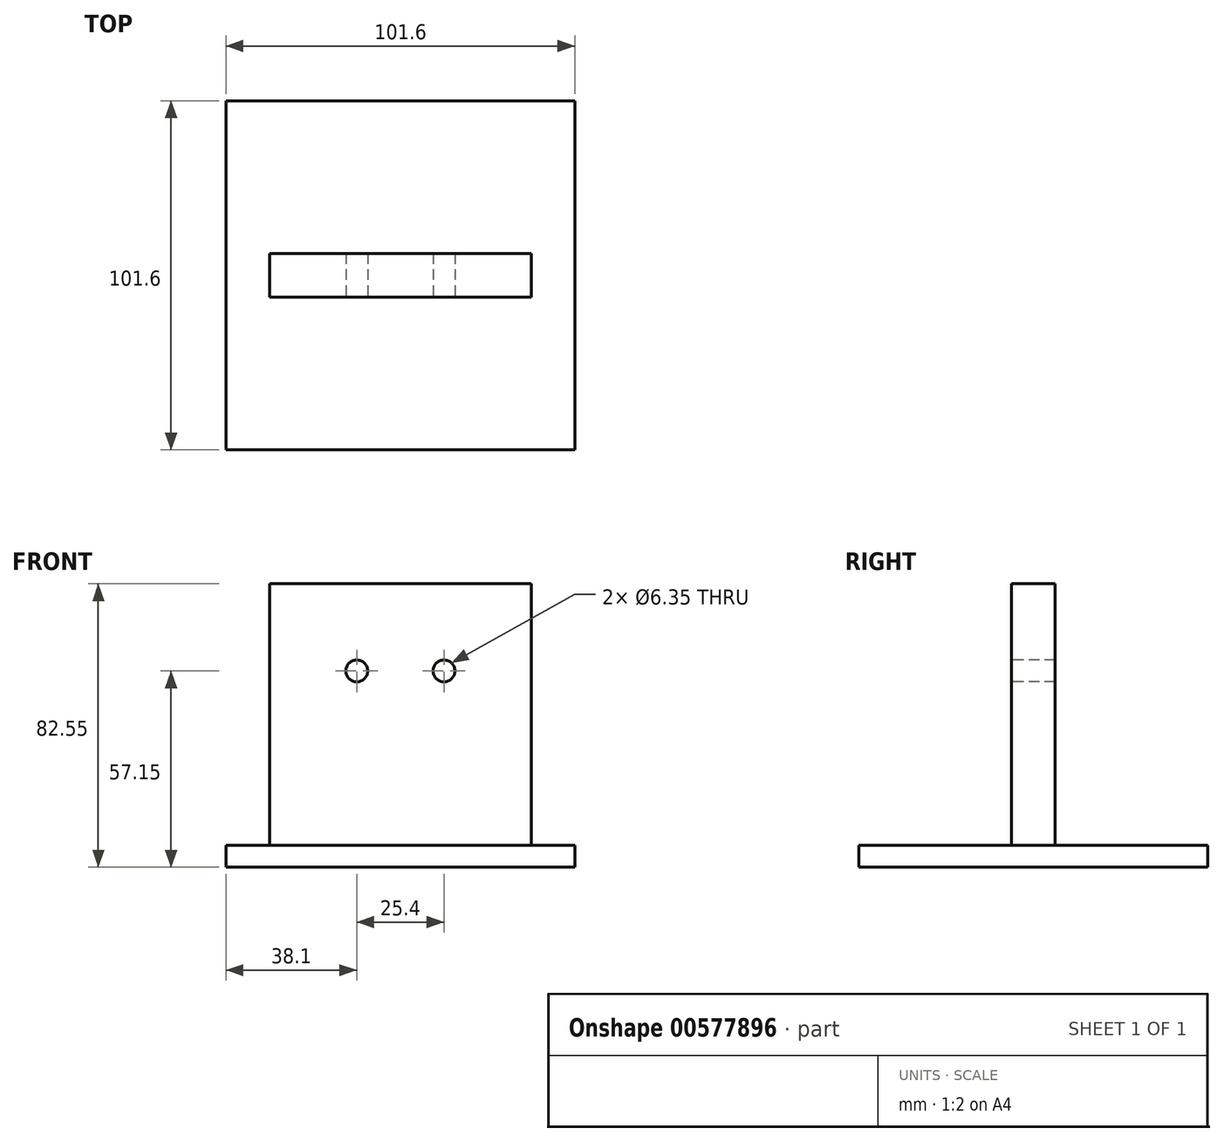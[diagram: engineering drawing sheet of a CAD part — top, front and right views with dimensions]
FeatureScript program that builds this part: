
annotation { "Feature Type Name" : "Feature", "Feature Type Description" : "" }
export const myFeature = defineFeature(function(context is Context, id is Id, definition is map)
    precondition{}
    {
        {
            var Q0;
            Q0=qCreatedBy(makeId("Top.planeOp"),FACE);
            var sketch = newSketch(context, id + "F0", { "sketchPlane" : qUnion([Q0])});
            skLineSegment(sketch, "E0.bottom", {"start": v(50.8, -50.8) * mm, "end": v(-50.8, -50.8) * mm});
            skLineSegment(sketch, "E0.top", {"start": v(50.8, 50.8) * mm, "end": v(-50.8, 50.8) * mm});
            skLineSegment(sketch, "E0.left", {"start": v(50.8, -50.8) * mm, "end": v(50.8, 50.8) * mm});
            skLineSegment(sketch, "E0.right", {"start": v(-50.8, -50.8) * mm, "end": v(-50.8, 50.8) * mm});
            skPoint(sketch, "E0.middle", {"position": v(0, 0) * mm});
            skSolve(sketch);
        }
        {
            var Q0;
            Q0=makeQuery(id+"F0.imprint","IMPRINT",FACE,{"disambiguationData":[TD([[makeQuery(id+"F0.imprint","IMPRINT",EDGE,{"derivedFrom":sQuery(id+"F0.wireOp",EDGE,"E0.bottom")}),-1.0]])]});
            extrude(context, id + "F1", {"entities" : qUnion([Q0]), "depth" : 6.35 * mm, "offsetDistance" : 25.4 * mm});
        }
        {
            var Q0;
            Q0=makeQuery(id+"F1.opExtrude","CAP_FACE",FACE,{"disambiguationData":[OSD([sQuery(id+"F0.wireOp",EDGE,"E0.bottom"),sQuery(id+"F0.wireOp",EDGE,"E0.top"),sQuery(id+"F0.wireOp",EDGE,"E0.left"),sQuery(id+"F0.wireOp",EDGE,"E0.right")])],"isStart":false});
            var sketch = newSketch(context, id + "F2", { "sketchPlane" : qUnion([Q0])});
            skLineSegment(sketch, "E1.bottom", {"start": v(38.1, 6.35) * mm, "end": v(-38.1, 6.35) * mm});
            skLineSegment(sketch, "E1.top", {"start": v(38.1, -6.35) * mm, "end": v(-38.1, -6.35) * mm});
            skLineSegment(sketch, "E1.left", {"start": v(38.1, 6.35) * mm, "end": v(38.1, -6.35) * mm});
            skLineSegment(sketch, "E1.right", {"start": v(-38.1, 6.35) * mm, "end": v(-38.1, -6.35) * mm});
            skPoint(sketch, "E1.middle", {"position": v(0, 0) * mm});
            skSolve(sketch);
        }
        {
            var Q0;
            Q0=makeQuery(id+"F2.imprint","IMPRINT",FACE,{"disambiguationData":[TD([[makeQuery(id+"F2.imprint","IMPRINT",EDGE,{"derivedFrom":sQuery(id+"F2.wireOp",EDGE,"E1.bottom")}),1.0]])]});
            extrude(context, id + "F3", {"entities" : qUnion([Q0]), "operationType" : NewBodyOperationType.ADD, "depth" : 76.2 * mm, "offsetDistance" : 25.4 * mm});
        }
        {
            var Q0;
            Q0=makeQuery(id+"F3.opExtrude","SWEPT_FACE",FACE,{"disambiguationData":[OSD([sQuery(id+"F2.wireOp",EDGE,"E1.top")])]});
            var sketch = newSketch(context, id + "F4", { "sketchPlane" : qUnion([Q0])});
            skLineSegment(sketch, "E2", {"start": v(-12.7, 57.15) * mm, "end": v(12.7, 57.15) * mm, "construction": true});
            skPoint(sketch, "E3", {"position": v(-12.7, 57.15) * mm});
            skPoint(sketch, "E4", {"position": v(12.7, 57.15) * mm});
            skSolve(sketch);
        }
        {
            var Q0;
            Q0=sQuery(id+"F4.wireOp",VERTEX,"E3");
            var Q1;
            Q1=sQuery(id+"F4.wireOp",VERTEX,"E4");
            var Q2;
            Q2=makeQuery(id+"F1.opExtrude","SWEPT_BODY",BODY,{"disambiguationData":[OSD([sQuery(id+"F0.wireOp",EDGE,"E0.bottom"),sQuery(id+"F0.wireOp",EDGE,"E0.top"),sQuery(id+"F0.wireOp",EDGE,"E0.left"),sQuery(id+"F0.wireOp",EDGE,"E0.right")])]});
            hole(context, id + "F5", {"style" : HoleStyle.SIMPLE, "endStyle" : HoleEndStyle.THROUGH, "holeDiameter" : 6.35 * mm, "isTappedThrough" : true, "tappedDepth" : 12.7 * mm, "tapClearance" : 3, "locations" : qUnion([Q0, Q1]), "scope" : qUnion([Q2])});
        }
    });
